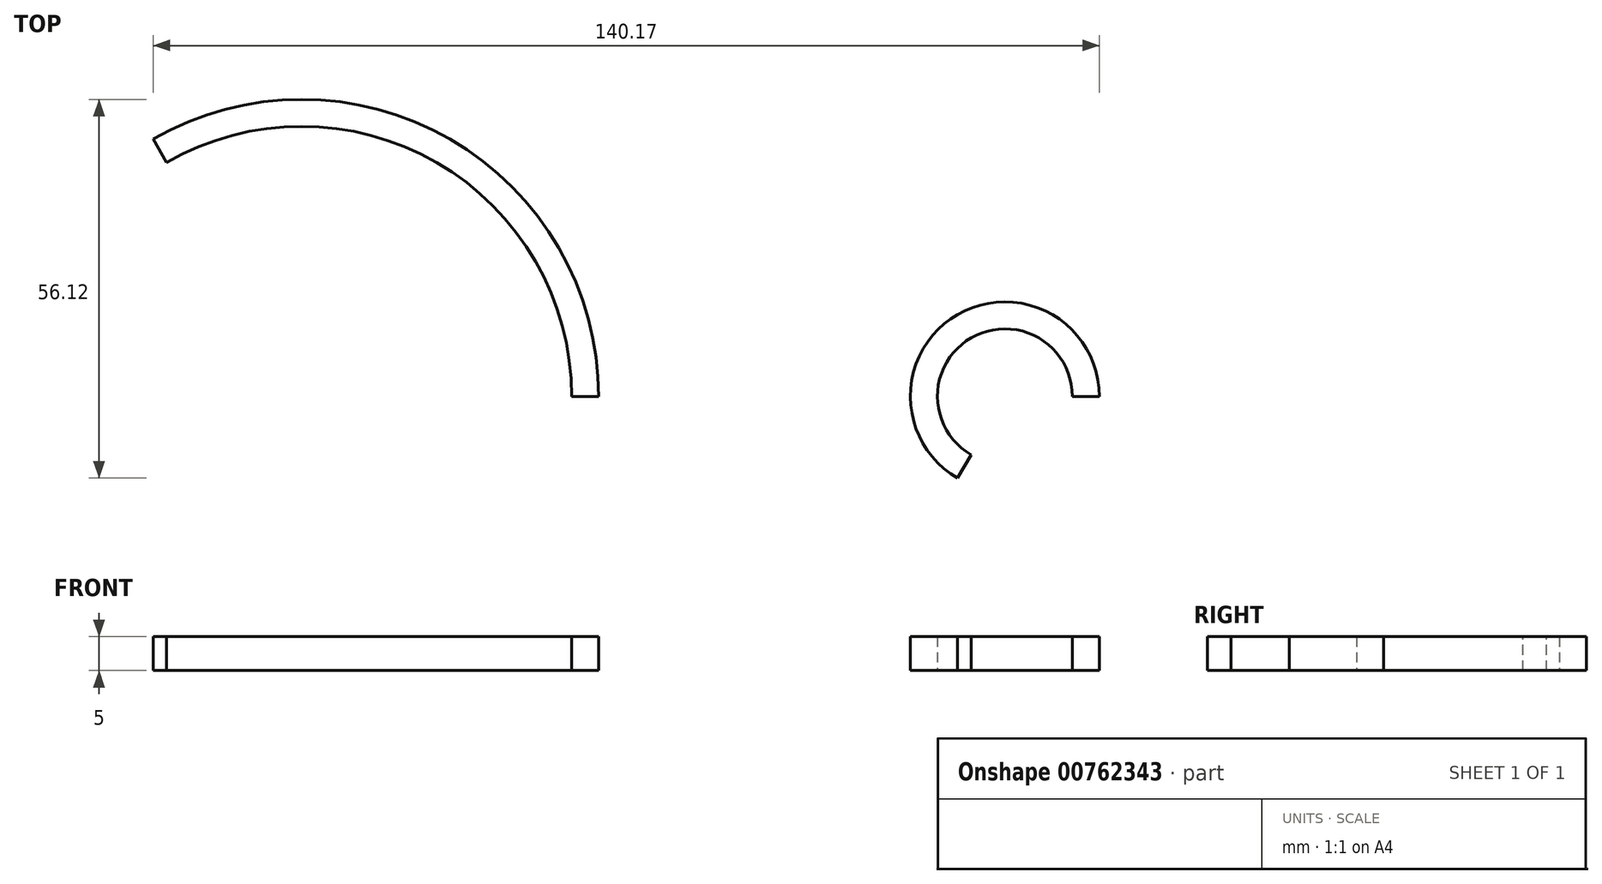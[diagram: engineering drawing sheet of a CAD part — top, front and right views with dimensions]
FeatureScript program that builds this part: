
annotation { "Feature Type Name" : "Feature", "Feature Type Description" : "" }
export const myFeature = defineFeature(function(context is Context, id is Id, definition is map)
    precondition{}
    {
        {
            var Q0;
            Q0=qCreatedBy(makeId("Front.planeOp"),FACE);
            var sketch = newSketch(context, id + "F0", { "sketchPlane" : qUnion([Q0])});
            skLineSegment(sketch, "E0.bottom", {"start": v(57.9, 0) * mm, "end": v(53.9, 0) * mm});
            skLineSegment(sketch, "E0.top", {"start": v(57.9, 5) * mm, "end": v(53.9, 5) * mm});
            skLineSegment(sketch, "E0.left", {"start": v(57.9, 0) * mm, "end": v(57.9, 5) * mm});
            skLineSegment(sketch, "E0.right", {"start": v(53.9, 0) * mm, "end": v(53.9, 5) * mm});
            skLineSegment(sketch, "E1", {"start": v(53.9, 0) * mm, "end": v(43.9, 0) * mm});
            skLineSegment(sketch, "E2", {"start": v(43.9, 0) * mm, "end": v(43.9, 14.22) * mm});
            skSolve(sketch);
        }
        {
            var Q0;
            Q0 = qSketchRegion(id + "F0", true);
            var Q1;
            Q1=sQuery(id+"F0.wireOp",EDGE,"E2");
            revolve(context, id + "F1", {"surfaceOperationType" : NewSurfaceOperationType.NEW, "entities" : qUnion([Q0]), "axis" : qUnion([Q1]), "revolveType" : RevolveType.ONE_DIRECTION, "angle" : 240 * degree});
        }
        {
            var Q0;
            Q0=qCreatedBy(makeId("Front.planeOp"),FACE);
            var sketch = newSketch(context, id + "F2", { "sketchPlane" : qUnion([Q0])});
            skLineSegment(sketch, "E3.bottom", {"start": v(-16.26, 0) * mm, "end": v(-20.26, 0) * mm});
            skLineSegment(sketch, "E3.top", {"start": v(-16.26, 5) * mm, "end": v(-20.26, 5) * mm});
            skLineSegment(sketch, "E3.left", {"start": v(-16.26, 0) * mm, "end": v(-16.26, 5) * mm});
            skLineSegment(sketch, "E3.right", {"start": v(-20.26, 0) * mm, "end": v(-20.26, 5) * mm});
            skLineSegment(sketch, "E4", {"start": v(-20.26, 0) * mm, "end": v(-60.26, 0) * mm});
            skLineSegment(sketch, "E5", {"start": v(-60.26, 0) * mm, "end": v(-60.26, 15.64) * mm});
            skSolve(sketch);
        }
        {
            var Q0;
            Q0 = qSketchRegion(id + "F2", true);
            var Q1;
            Q1=sQuery(id+"F2.wireOp",EDGE,"E5");
            revolve(context, id + "F3", {"surfaceOperationType" : NewSurfaceOperationType.NEW, "entities" : qUnion([Q0]), "axis" : qUnion([Q1]), "revolveType" : RevolveType.ONE_DIRECTION, "angle" : 120 * degree});
        }
    });
